# Revit family: HCL_Latchways_BaluAndGuardSym_VersiRail_Folding
name_source: partatom
category: Railings
revit_build: Autodesk Revit 2014 (Build: 20130308_1515(x64)
units: mm (PartAtom-declared; Revit-internal decimal feet)

## types (9) — shared parameters
AssetType = Movable
Default Elevation = 1219 mm
Description = Latchways ManSafe® for Roofing, using VersiRail
Diameter = 40 mm  [stored 0.131234 ft]
DurationUnit = year
Height = 1150 mm
IfcExportAs = GUARDRAIL
IfcExportType = IfcRailing
Installer Info = https://www.hclsafety.com
Installer Website = https://www.hclsafety.com
IsExternal = Yes
ManufacturerURL = www.latchways.com
Material = Handrails & Uprights: Aluminium; Counterweight: Concrete filled HDPE with UV protection
ModelReference = VersiRail - Straight Freestanding Foldable assembly
NBSDescription = Balustrade and guarding system
NBSReference = 25-25-10/110
NominalHeight = 1150 mm
NominalLength = 1310 mm  [stored 4.2979 ft]
NominalWidth = 253 mm  [stored 0.830052 ft]
ProductInformation = www.latchways.com/BIM/Latchways_FreestandingFoldingStraightVersiRail_Datasheet.pdf
RailAngle = 90.00°
RailMaterial = LWplc_Latchwaysplc_Aluminium_Polished
Size = 235 x 1310 x 1150 mm
SupportMaterial = LWplc_Latchwaysplc_Aluminium_Polished
URL = www.latchways.com
Uniclass2 = Ss_25_15_60_05
Version = 1
WarrantyDurationUnit = year

## per-type parameters (varying)
| type | BIMObjectName | CounterWeightMaterial | CurvedUpright | InclinedUpright | LeftLeg | ManufacturerName | Model | ModelNumber | RightLeg | StraightLeg | StraightUpright |
| BalustradeAndGuardingSystem_VersiRailFolding_CurvedLeft_MSA_Latchways | HCL_Latchways_BalustradeAndGuardingSystem_VersiRailFolding_CurvedLeft | LWplc_Latchwaysplc_VersiRailWeight | Yes | No | Yes | MSA Latchways | 22303-00+22080-01 | 22303-00+22080-01 | No | No | No |
| BalustradeAndGuardingSystem_VersiRailFolding_CurvedRight_MSA_Latchways | HCL_Latchways_BalustradeAndGuardingSystem_VersiRailFolding_CurvedRight | LWplc_Latchwaysplc_VersiRailWeight | Yes | No | No | MSA_Latchways | 22304-00+22080-01 | 22304-00+22080-01 | Yes | No | No |
| BalustradeAndGuardingSystem_VersiRailFolding_CurvedStraight_MSA_Latchways | HCL_Latchwaysplc_BalustradeAndGuardingSystem_VersiRailFolding_CurvedStraight | LWplc_Latchwaysplc_VersiRailWeight | Yes | No | No | MSA Latchways | 22303-00+22080-01 | 22303-00+22080-01 | No | Yes | No |
| BalustradeAndGuardingSystem_VersiRailFolding_InclinedLeft_MSA_Latchways | HCL_Latchways_BalustradeAndGuardingSystem_VersiRailFolding_InclinedLeft | LWplc_Latchwaysplc_VersiRailWeight | No | Yes | Yes | MSA Latchways | 22303-00+22080-01 | 22303-00+22080-01 | No | No | No |
| BalustradeAndGuardingSystem_VersiRailFolding_InclinedRight_MSA_Latchways | HCL_Latchways_BalustradeAndGuardingSystem_VersiRailFolding_InclinedRight | LWplc_Latchwaysplc_VersiRailWeight | No | Yes | No | MSA Latchways | 22304-00+22080-01 | 22304-00+22080-01 | Yes | No | No |
| BalustradeAndGuardingSystem_VersiRailFolding_InclinedStraight_MSA_Latchways | HCL_Latchways_BalustradeAndGuardingSystem_VersiRailFolding_InclinedStraight | LWplc_Latchwaysplc_VersiRailWeight | No | Yes | No | MSA Latchways | 22303-00+22080-01 | 22303-00+22080-01 | No | Yes | No |
| BalustradeAndGuardingSystem_VersiRailFolding_StraightLeft_MSA_Latchways | HCL_Latchways_BalustradeAndGuardingSystem_VersiRailFolding_StraightLeft | LWplc_Latchwaysplc_VersiRailWeight | No | No | Yes | MSA Latchways | 22303-00+22080-01 | 22303-00+22080-01 | No | No | Yes |
| BalustradeAndGuardingSystem_VersiRailFolding_StraightRight_MSA_Latchways | HCL_Latchways_BalustradeAndGuardingSystem_VersiRailFolding_StraightRight | LWplc_Latchwaysplc_VersiRailWeight | No | No | No | MSA Latchways | 22304-00+22080-01 | 22304-00+22080-01 | Yes | No | Yes |
| BalustradeAndGuardingSystem_VersiRailFolding_StraightStraight_MSA_Latchways | HCL_Latchwaysplc_BalustradeAndGuardingSystem_VersiRailFolding_StraightStraight | LWplc_Latchwaysplc_Plastic_VersiRailWeight | No | No | No | MSA Latchways | 22304-00+22080-01 | 22304-00+22080-01 | No | Yes | Yes |

note: column(s) folded — value = type name in every type: Name

note: [stored X ft] marks values corroborated as IEEE doubles in the binary element streams (Revit-internal decimal feet)

## geometry (parser evidence)
native form markers: Blend x6, Sweep x10
no freeform markers — native parametric forms only
